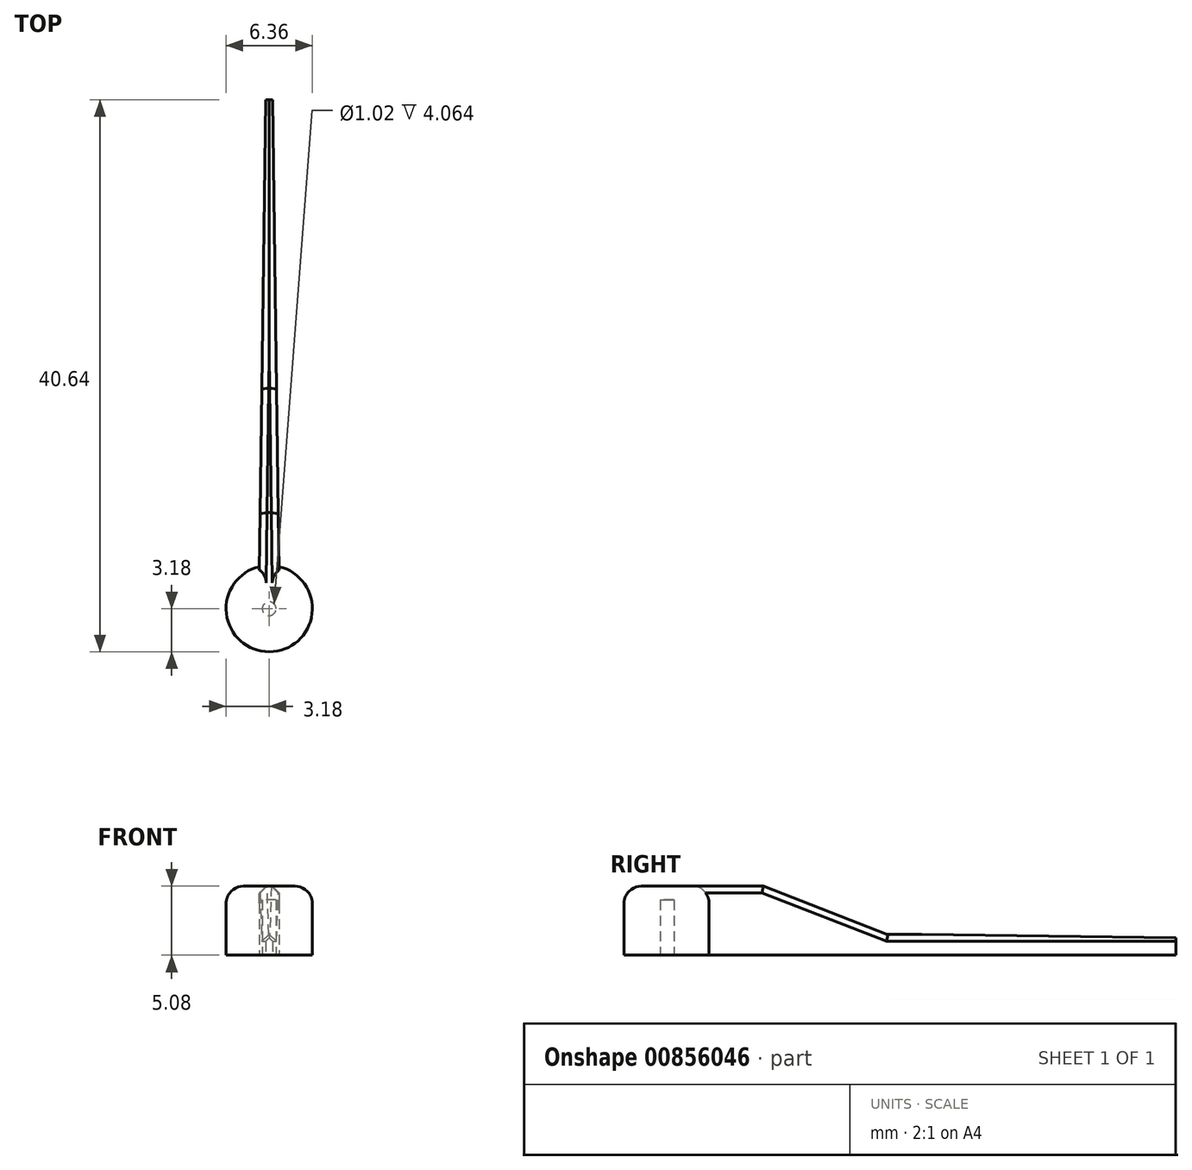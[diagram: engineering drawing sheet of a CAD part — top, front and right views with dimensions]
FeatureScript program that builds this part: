
annotation { "Feature Type Name" : "Feature", "Feature Type Description" : "" }
export const myFeature = defineFeature(function(context is Context, id is Id, definition is map)
    precondition{}
    {
        {
            var Q0;
            Q0=qCreatedBy(makeId("Top.planeOp"),FACE);
            var sketch = newSketch(context, id + "F0", { "sketchPlane" : qUnion([Q0])});
            skLineSegment(sketch, "E0", {"start": v(0, 0) * mm, "end": v(-0.76, 0) * mm});
            skLineSegment(sketch, "E1", {"start": v(0, 0) * mm, "end": v(0.76, 0) * mm});
            skCircle(sketch, "E2", {"center": v(0, 0) * mm, "radius": 3.18 * mm});
            skLineSegment(sketch, "E3", {"start": v(-0.76, 0) * mm, "end": v(-0.25, 37.46) * mm});
            skLineSegment(sketch, "E4", {"start": v(0.76, 0) * mm, "end": v(0.25, 37.46) * mm});
            skLineSegment(sketch, "E5", {"start": v(0.25, 37.46) * mm, "end": v(-0.25, 37.46) * mm});
            skSolve(sketch);
        }
        {
            var Q0;
            Q0=qSketchRegion(id+"F0",true);
            var Q1;
            {var subQ0=sQuery(id+"F0.wireOp",EDGE,"E1");var subQ1=sQuery(id+"F0.wireOp",EDGE,"E0");var subQ2=makeQuery(id+"F0.imprint","INTERSECT",VERTEX,{"derivedFrom":[subQ1,subQ0]});Q1=makeQuery(id+"F0.imprint","IMPRINT",FACE,{"disambiguationData":[TD([[makeQuery(id+"F0.imprint","IMPRINT",EDGE,{"disambiguationData":[TD([[subQ2,-1.0]])],"derivedFrom":subQ1}),-1.0]])]});}
            var Q2;
            {var subQ0=sQuery(id+"F0.wireOp",EDGE,"E1");var subQ1=sQuery(id+"F0.wireOp",EDGE,"E0");var subQ2=makeQuery(id+"F0.imprint","INTERSECT",VERTEX,{"derivedFrom":[subQ1,subQ0]});Q2=makeQuery(id+"F0.imprint","IMPRINT",FACE,{"disambiguationData":[TD([[makeQuery(id+"F0.imprint","IMPRINT",EDGE,{"disambiguationData":[TD([[subQ2,-1.0]])],"derivedFrom":subQ1}),1.0]])]});}
            extrude(context, id + "F1", {"entities" : qUnion([Q0, Q1, Q2]), "depth" : 5.08 * mm, "offsetDistance" : 25.4 * mm});
        }
        {
            var Q0;
            Q0=makeQuery(id+"F1.opExtrude","CAP_EDGE",EDGE,{"disambiguationData":[OSD([sQuery(id+"F0.wireOp",EDGE,"E2")])],"isStart":false});
            fillet(context, id + "F2", {"entities" : qUnion([Q0]), "radius" : 1.27 * mm, "tangentPropagation" : true, "allowEdgeOverflow" : false});
        }
        {
            var Q0;
            Q0=qCreatedBy(makeId("Top.planeOp"),FACE);
            var sketch = newSketch(context, id + "F3", { "sketchPlane" : qUnion([Q0])});
            skCircle(sketch, "E6", {"center": v(0, 0) * mm, "radius": 0.5 * mm});
            skSolve(sketch);
        }
        {
            var Q0;
            Q0=qSketchRegion(id+"F3",true);
            extrude(context, id + "F4", {"entities" : qUnion([Q0]), "operationType" : NewBodyOperationType.REMOVE, "depth" : 4.06 * mm, "offsetDistance" : 25.4 * mm});
        }
        {
            var Q0;
            Q0=qCreatedBy(makeId("Right.planeOp"),FACE);
            var sketch = newSketch(context, id + "F5", { "sketchPlane" : qUnion([Q0])});
            skLineSegment(sketch, "E7", {"start": v(-3.41, 9.15) * mm, "end": v(16.24, 1.52) * mm});
            skLineSegment(sketch, "E8", {"start": v(16.24, 1.52) * mm, "end": v(47.1, 1.52) * mm});
            skLineSegment(sketch, "E9", {"start": v(47.1, 1.52) * mm, "end": v(47.1, 6.88) * mm});
            skLineSegment(sketch, "E10", {"start": v(47.1, 6.88) * mm, "end": v(-3.41, 9.15) * mm});
            skSolve(sketch);
        }
        {
            var Q0;
            Q0=qSketchRegion(id+"F5",true);
            extrude(context, id + "F6", {"entities" : qUnion([Q0]), "operationType" : NewBodyOperationType.REMOVE, "depth" : 5.08 * mm, "offsetDistance" : 25.4 * mm, "hasSecondDirection" : true, "secondDirectionOppositeDirection" : true, "secondDirectionDepth" : 5.08 * mm});
        }
        {
            var Q0;
            Q0=makeQuery(id+"F6.boolean.opBoolean","INTERSECT",EDGE,{"derivedFrom":[makeQuery(id+"F1.opExtrude","SWEPT_FACE",FACE,{"disambiguationData":[OSD([sQuery(id+"F0.wireOp",EDGE,"E4")])]}),makeQuery(id+"F6.opExtrude","SWEPT_FACE",FACE,{"disambiguationData":[OSD([sQuery(id+"F5.wireOp",EDGE,"E8")])]})]});
            var Q1;
            Q1=makeQuery(id+"F6.boolean.opBoolean","INTERSECT",EDGE,{"derivedFrom":[makeQuery(id+"F1.opExtrude","SWEPT_FACE",FACE,{"disambiguationData":[OSD([sQuery(id+"F0.wireOp",EDGE,"E3")])]}),makeQuery(id+"F6.opExtrude","SWEPT_FACE",FACE,{"disambiguationData":[OSD([sQuery(id+"F5.wireOp",EDGE,"E8")])]})]});
            var Q2;
            Q2=makeQuery(id+"F6.boolean.opBoolean","INTERSECT",EDGE,{"derivedFrom":[makeQuery(id+"F1.opExtrude","SWEPT_FACE",FACE,{"disambiguationData":[OSD([sQuery(id+"F0.wireOp",EDGE,"E4")])]}),makeQuery(id+"F6.opExtrude","SWEPT_FACE",FACE,{"disambiguationData":[OSD([sQuery(id+"F5.wireOp",EDGE,"E7")])]})]});
            var Q3;
            Q3=makeQuery(id+"F6.boolean.opBoolean","INTERSECT",EDGE,{"derivedFrom":[makeQuery(id+"F1.opExtrude","SWEPT_FACE",FACE,{"disambiguationData":[OSD([sQuery(id+"F0.wireOp",EDGE,"E3")])]}),makeQuery(id+"F6.opExtrude","SWEPT_FACE",FACE,{"disambiguationData":[OSD([sQuery(id+"F5.wireOp",EDGE,"E7")])]})]});
            var Q4;
            Q4=makeQuery(id+"F1.opExtrude","CAP_EDGE",EDGE,{"disambiguationData":[OSD([sQuery(id+"F0.wireOp",EDGE,"E4")])],"isStart":false});
            var Q5;
            Q5=makeQuery(id+"F1.opExtrude","CAP_EDGE",EDGE,{"disambiguationData":[OSD([sQuery(id+"F0.wireOp",EDGE,"E3")])],"isStart":false});
            var Q6;
            Q6=makeQuery(id+"F6.boolean.opBoolean","INTERSECT",EDGE,{"derivedFrom":[makeQuery(id+"F1.opExtrude","SWEPT_FACE",FACE,{"disambiguationData":[OSD([sQuery(id+"F0.wireOp",EDGE,"E5")])]}),makeQuery(id+"F6.opExtrude","SWEPT_FACE",FACE,{"disambiguationData":[OSD([sQuery(id+"F5.wireOp",EDGE,"E8")])]})]});
            chamfer(context, id + "F7", {"entities" : qUnion([Q0, Q1, Q2, Q3, Q4, Q5, Q6]), "width" : 0.5 * mm, "tangentPropagation" : true});
        }
    });
